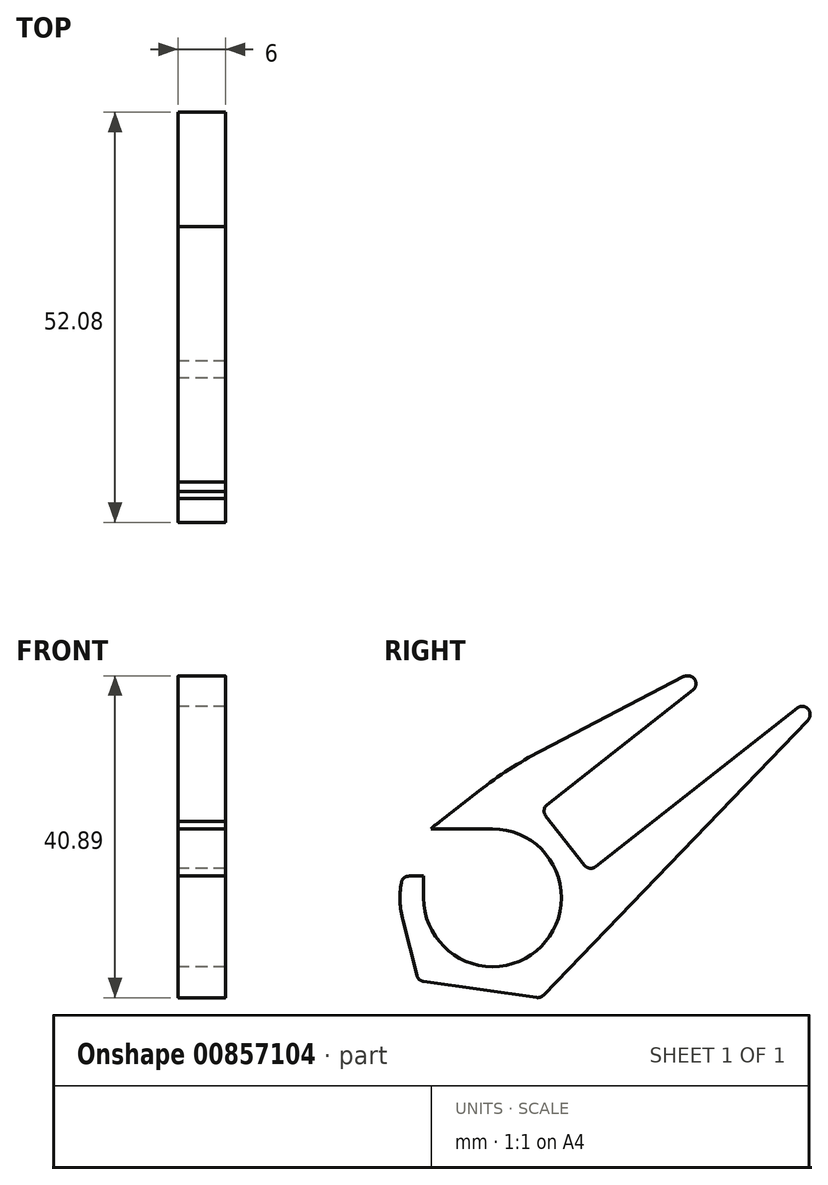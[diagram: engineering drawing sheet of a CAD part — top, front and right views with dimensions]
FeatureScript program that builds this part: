
annotation { "Feature Type Name" : "Feature", "Feature Type Description" : "" }
export const myFeature = defineFeature(function(context is Context, id is Id, definition is map)
    precondition{}
    {
        {
            var Q0;
            Q0=qCreatedBy(makeId("Right.planeOp"),FACE);
            var sketch = newSketch(context, id + "F0", { "sketchPlane" : qUnion([Q0])});
            skArc(sketch, "E0", {"start": v(-8.75, 0) * mm, "mid": v(6.19, -6.19) * mm, "end": v(0, 8.75) * mm});
            skLineSegment(sketch, "E1.bottom", {"start": v(0, 8.75) * mm, "end": v(-122.25, 8.75) * mm, "construction": true});
            skLineSegment(sketch, "E1.top", {"start": v(-11.75, 5.75) * mm, "end": v(-122.25, 5.75) * mm, "construction": true});
            skLineSegment(sketch, "E1.right", {"start": v(-122.25, 8.75) * mm, "end": v(-122.25, 5.75) * mm, "construction": true});
            skLineSegment(sketch, "E2", {"start": v(8.75, 0) * mm, "end": v(8.75, 20.78) * mm, "construction": true});
            skLineSegment(sketch, "E3", {"start": v(-8.75, 0) * mm, "end": v(-8.75, 2.75) * mm, "construction": true});
            skPoint(sketch, "E4.visualSharp", {"position": v(-8.75, 5.75) * mm});
            skArc(sketch, "E4.filletArc", {"start": v(-8.75, 2.75) * mm, "mid": v(-9.63, 4.87) * mm, "end": v(-11.75, 5.75) * mm, "construction": true});
            skLineSegment(sketch, "E5", {"start": v(-122.25, 5.75) * mm, "end": v(120.77, -23.2) * mm, "construction": true});
            skArc(sketch, "E6", {"start": v(-6.66, 9.68) * mm, "mid": v(-7.27, 9.23) * mm, "end": v(-7.84, 8.75) * mm});
            skLineSegment(sketch, "E7", {"start": v(0, 0) * mm, "end": v(69.32, 54.56) * mm, "construction": true});
            skLineSegment(sketch, "E8", {"start": v(6.93, 11.81) * mm, "end": v(25.46, 26.4) * mm});
            skLineSegment(sketch, "E9", {"start": v(13.11, 3.96) * mm, "end": v(38.72, 24.11) * mm});
            skLineSegment(sketch, "E10", {"start": v(-7.84, 8.75) * mm, "end": v(-1.7, 13.58) * mm});
            skLineSegment(sketch, "E11", {"start": v(6.76, 10.41) * mm, "end": v(11.7, 4.12) * mm});
            skArc(sketch, "E12.trimOffspring", {"start": v(9.23, 7.27) * mm, "mid": v(9, 7.56) * mm, "end": v(8.75, 7.84) * mm});
            skArc(sketch, "E13.filletArc", {"start": v(6.93, 11.81) * mm, "mid": v(6.55, 11.15) * mm, "end": v(6.76, 10.41) * mm});
            skArc(sketch, "E14.filletArc", {"start": v(11.7, 4.12) * mm, "mid": v(12.37, 3.75) * mm, "end": v(13.11, 3.96) * mm});
            skLineSegment(sketch, "E15", {"start": v(24.96, 28.18) * mm, "end": v(24.85, 28.2) * mm});
            skLineSegment(sketch, "E16", {"start": v(40.33, 23.2) * mm, "end": v(40.32, 23.13) * mm});
            skLineSegment(sketch, "E17", {"start": v(6.14, 18.64) * mm, "end": v(24.27, 28.09) * mm});
            skLineSegment(sketch, "E18", {"start": v(16.49, -1.95) * mm, "end": v(40.05, 22.55) * mm});
            skLineSegment(sketch, "E19", {"start": v(11.7, 4.12) * mm, "end": v(16.49, -1.95) * mm, "construction": true});
            skLineSegment(sketch, "E20", {"start": v(6.76, 10.41) * mm, "end": v(1.98, 16.48) * mm, "construction": true});
            skPoint(sketch, "E21.visualSharp", {"position": v(24.55, 28.23) * mm});
            skArc(sketch, "E21.filletArc", {"start": v(24.85, 28.2) * mm, "mid": v(24.56, 28.18) * mm, "end": v(24.27, 28.09) * mm});
            skPoint(sketch, "E22.visualSharp", {"position": v(27.36, 27.9) * mm});
            skArc(sketch, "E22.filletArc", {"start": v(25.46, 26.4) * mm, "mid": v(25.8, 27.46) * mm, "end": v(24.96, 28.18) * mm});
            skPoint(sketch, "E23.visualSharp", {"position": v(40.61, 25.6) * mm});
            skArc(sketch, "E23.filletArc", {"start": v(40.33, 23.2) * mm, "mid": v(39.82, 24.2) * mm, "end": v(38.72, 24.11) * mm});
            skPoint(sketch, "E24.visualSharp", {"position": v(40.28, 22.8) * mm});
            skArc(sketch, "E24.filletArc", {"start": v(40.05, 22.55) * mm, "mid": v(40.23, 22.82) * mm, "end": v(40.32, 23.13) * mm});
            skPoint(sketch, "E25.visualSharp", {"position": v(1.98, 16.48) * mm});
            skArc(sketch, "E25.filletArc", {"start": v(6.14, 18.64) * mm, "mid": v(2.1, 16.3) * mm, "end": v(-1.7, 13.58) * mm});
            skLineSegment(sketch, "E26", {"start": v(0, 8.75) * mm, "end": v(-7.84, 8.75) * mm});
            skLineSegment(sketch, "E27", {"start": v(-7.84, 8.75) * mm, "end": v(11.32, -12.63) * mm, "construction": true});
            skLineSegment(sketch, "E28", {"start": v(-122.25, 5.75) * mm, "end": v(120.48, -29.24) * mm, "construction": true});
            skLineSegment(sketch, "E29", {"start": v(16.49, -1.95) * mm, "end": v(6.46, -12.38) * mm});
            skLineSegment(sketch, "E30", {"start": v(5.6, -12.68) * mm, "end": v(-1.68, -11.63) * mm});
            skLineSegment(sketch, "E31", {"start": v(-1.68, -11.63) * mm, "end": v(0, 0) * mm, "construction": true});
            skLineSegment(sketch, "E32", {"start": v(-1.68, -11.63) * mm, "end": v(-8.8, -10.6) * mm});
            skLineSegment(sketch, "E33", {"start": v(-9.62, -9.86) * mm, "end": v(-11.4, -2.88) * mm});
            skLineSegment(sketch, "E34", {"start": v(-8.75, 0) * mm, "end": v(-8.75, 2.75) * mm});
            skLineSegment(sketch, "E35", {"start": v(-10.6, 2.75) * mm, "end": v(-8.75, 2.75) * mm});
            skArc(sketch, "E36.trimOffspring", {"start": v(-11.6, 1.91) * mm, "mid": v(-11.74, -0.5) * mm, "end": v(-11.4, -2.88) * mm});
            skPoint(sketch, "E37.visualSharp", {"position": v(-11.42, 2.75) * mm});
            skArc(sketch, "E37.filletArc", {"start": v(-10.6, 2.75) * mm, "mid": v(-11.25, 2.51) * mm, "end": v(-11.6, 1.91) * mm});
            skPoint(sketch, "E38.visualSharp", {"position": v(-9.46, -10.5) * mm});
            skArc(sketch, "E38.filletArc", {"start": v(-9.62, -9.86) * mm, "mid": v(-9.32, -10.36) * mm, "end": v(-8.8, -10.6) * mm});
            skPoint(sketch, "E39.visualSharp", {"position": v(6.1, -12.75) * mm});
            skArc(sketch, "E39.filletArc", {"start": v(5.6, -12.68) * mm, "mid": v(6.07, -12.63) * mm, "end": v(6.46, -12.38) * mm});
            skSolve(sketch);
        }
        {
            var Q0;
            Q0 = qSketchRegion(id + "F0", true);
            extrude(context, id + "F1", {"entities" : qUnion([Q0]), "depth" : 6 * mm, "offsetDistance" : 25 * mm});
        }
    });
